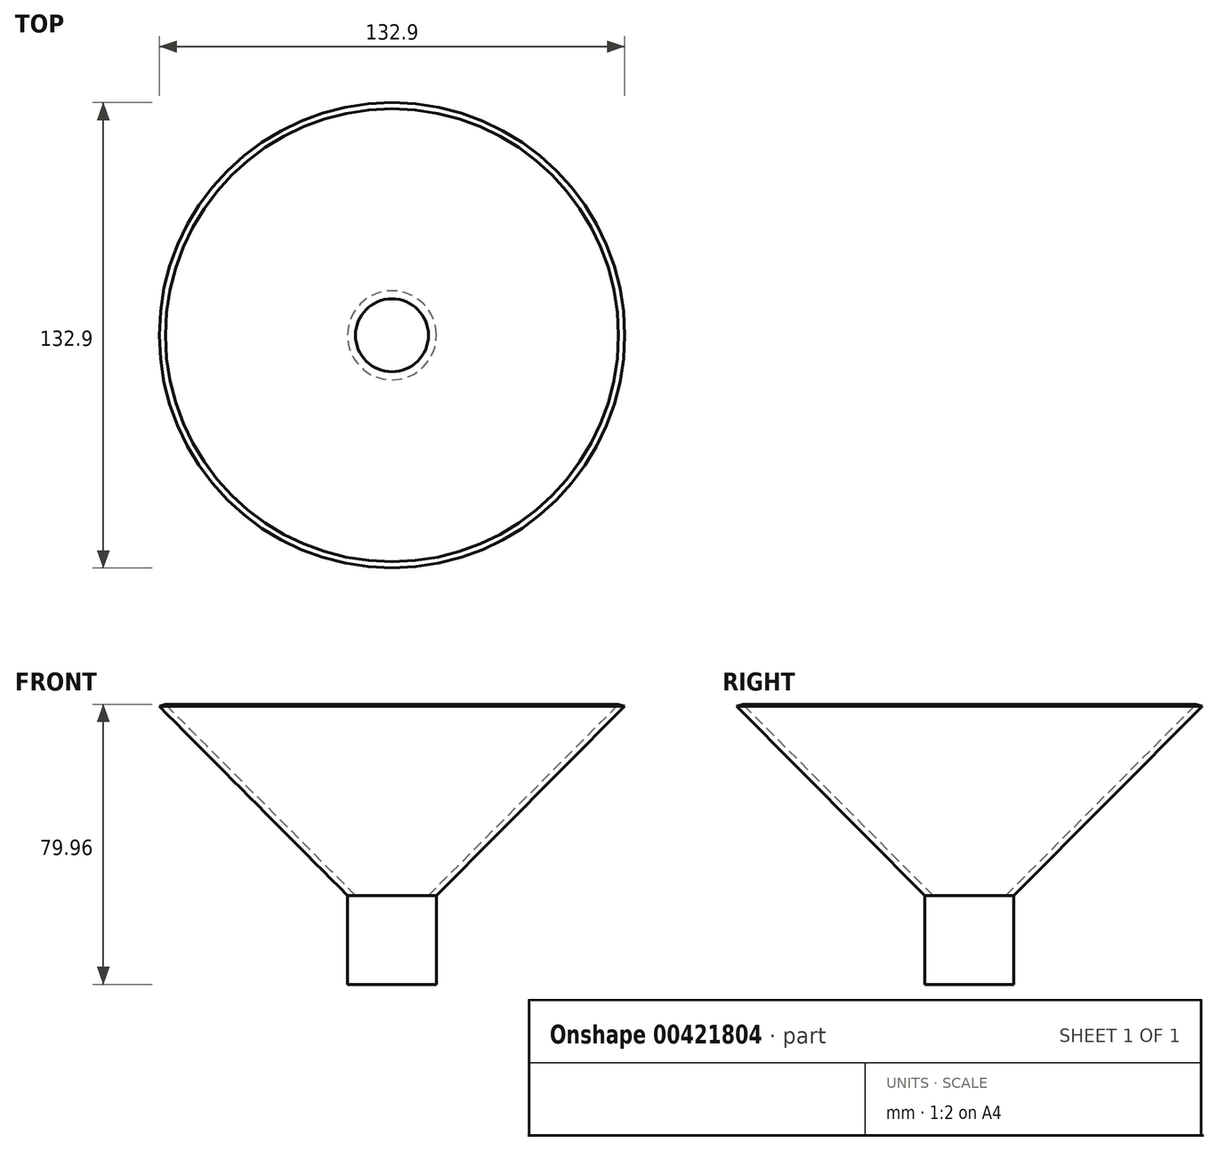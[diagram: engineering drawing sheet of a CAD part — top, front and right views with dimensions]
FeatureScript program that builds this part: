
annotation { "Feature Type Name" : "Feature", "Feature Type Description" : "" }
export const myFeature = defineFeature(function(context is Context, id is Id, definition is map)
    precondition{}
    {
        {
            var Q0;
            Q0=qCreatedBy(makeId("Front.planeOp"),FACE);
            var sketch = newSketch(context, id + "F0", { "sketchPlane" : qUnion([Q0])});
            skLineSegment(sketch, "E0", {"start": v(53.75, 54.02) * mm, "end": v(0, 0) * mm});
            skLineSegment(sketch, "E1", {"start": v(0, 0) * mm, "end": v(0, -25.4) * mm});
            skLineSegment(sketch, "E2", {"start": v(0, -25.4) * mm, "end": v(-12.7, -25.4) * mm});
            skLineSegment(sketch, "E3", {"start": v(-12.7, -25.4) * mm, "end": v(-12.7, 0) * mm});
            skLineSegment(sketch, "E4", {"start": v(-12.7, 0) * mm, "end": v(-2.3, 0) * mm});
            skLineSegment(sketch, "E5", {"start": v(-2.3, 0) * mm, "end": v(52, 54.56) * mm});
            skLineSegment(sketch, "E6", {"start": v(52, 54.56) * mm, "end": v(53.75, 54.02) * mm});
            skSolve(sketch);
        }
        {
            var Q0;
            Q0=makeQuery(id+"F0.imprint","IMPRINT",FACE,{"disambiguationData":[TD([[makeQuery(id+"F0.imprint","IMPRINT",EDGE,{"derivedFrom":sQuery(id+"F0.wireOp",EDGE,"E0")}),-1.0]])]});
            var Q1;
            Q1=sQuery(id+"F0.wireOp",EDGE,"E3");
            revolve(context, id + "F1", {"entities" : qUnion([Q0]), "axis" : qUnion([Q1]), "revolveType" : RevolveType.FULL});
        }
    });
